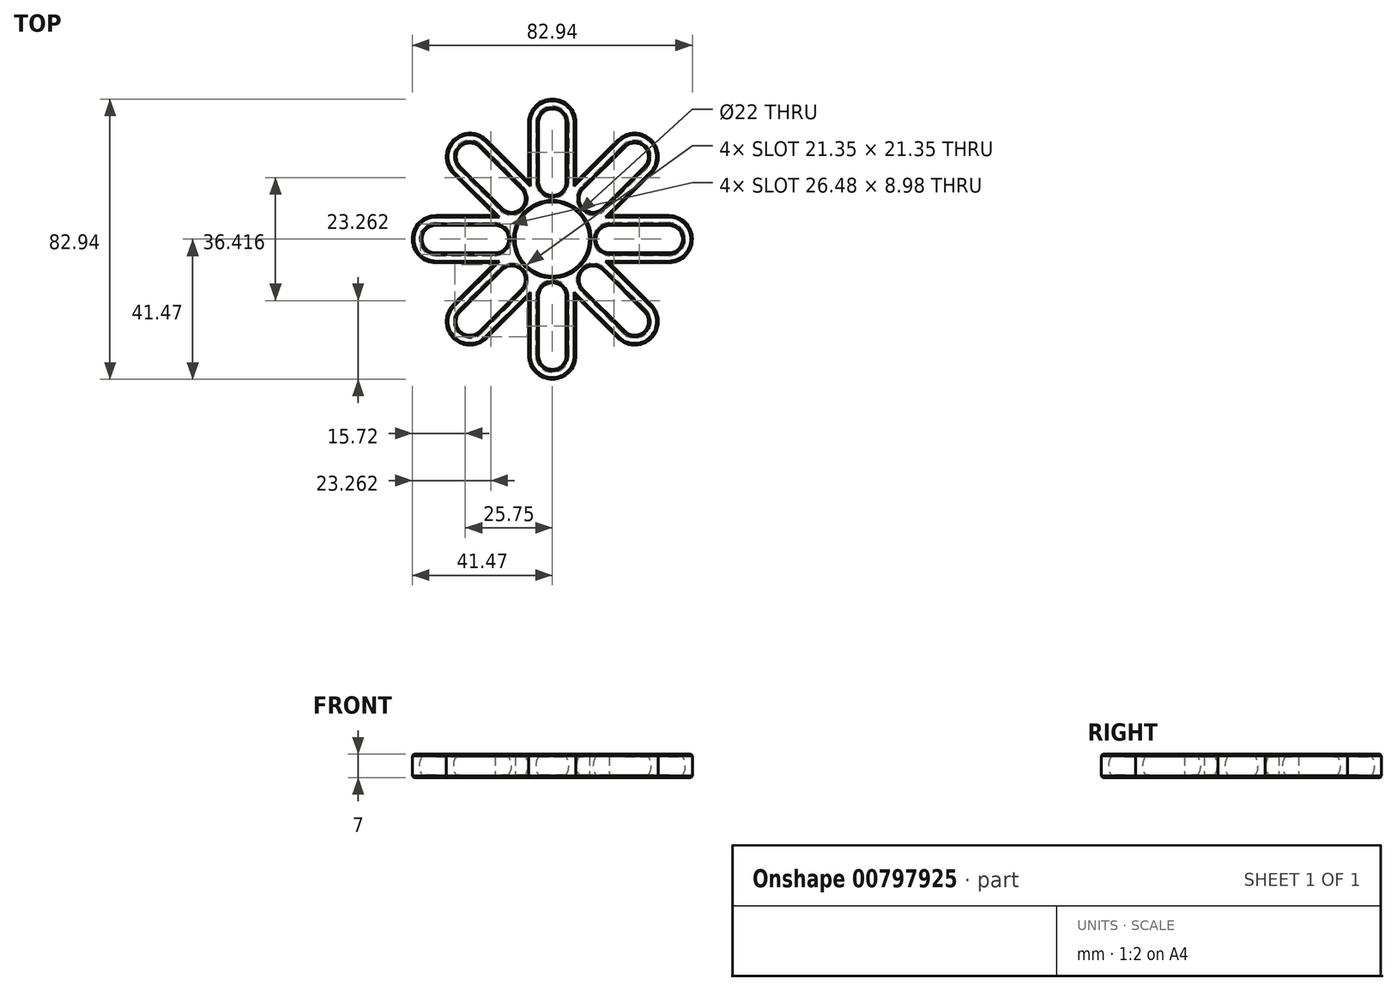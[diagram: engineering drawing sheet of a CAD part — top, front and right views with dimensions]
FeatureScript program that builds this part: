
annotation { "Feature Type Name" : "Feature", "Feature Type Description" : "" }
export const myFeature = defineFeature(function(context is Context, id is Id, definition is map)
    precondition{}
    {
        {
            var Q0;
            Q0=qCreatedBy(makeId("Top.planeOp"),FACE);
            var sketch = newSketch(context, id + "F0", { "sketchPlane" : qUnion([Q0])});
            skArc(sketch, "E0", {"start": v(7, 8.49) * mm, "mid": v(0, 11) * mm, "end": v(-7, 8.49) * mm});
            skArc(sketch, "E1", {"start": v(7, 12.12) * mm, "mid": v(0, 14) * mm, "end": v(-7, 12.12) * mm});
            skPoint(sketch, "E2", {"position": v(0, -24.5) * mm});
            skLineSegment(sketch, "E3", {"start": v(-7, 12.12) * mm, "end": v(-7, 34.47) * mm});
            skLineSegment(sketch, "E4", {"start": v(-7, 34.47) * mm, "end": v(7, 34.47) * mm});
            skLineSegment(sketch, "E5", {"start": v(7, 34.47) * mm, "end": v(7, 12.12) * mm});
            skArc(sketch, "E6", {"start": v(7, 34.47) * mm, "mid": v(0, 41.47) * mm, "end": v(-7, 34.47) * mm});
            skLineSegment(sketch, "E7", {"start": v(7, 12.12) * mm, "end": v(7, 8.49) * mm});
            skLineSegment(sketch, "E8", {"start": v(-7, 12.12) * mm, "end": v(-7, 8.49) * mm});
            skLineSegment(sketch, "E9", {"start": v(0, 0) * mm, "end": v(0, 68.94) * mm, "construction": true});
            skSolve(sketch);
        }
        {
            var Q0;
            Q0=makeQuery(id+"F0.imprint","IMPRINT",FACE,{"disambiguationData":[TD([[makeQuery(id+"F0.imprint","IMPRINT",EDGE,{"derivedFrom":sQuery(id+"F0.wireOp",EDGE,"E0")}),-1.0]])]});
            var Q1;
            {var subQ0=sQuery(id+"F0.wireOp",EDGE,"E3");Q1=makeQuery(id+"F0.imprint","IMPRINT",FACE,{"disambiguationData":[TD([[makeQuery(id+"F0.imprint","IMPRINT",EDGE,{"derivedFrom":subQ0}),-1.0]])]});}
            var Q2;
            Q2=makeQuery(id+"F0.imprint","IMPRINT",FACE,{"disambiguationData":[TD([[makeQuery(id+"F0.imprint","IMPRINT",EDGE,{"derivedFrom":sQuery(id+"F0.wireOp",EDGE,"E4")}),1.0]])]});
            extrude(context, id + "F1", {"entities" : qUnion([Q0, Q1, Q2]), "endBound" : BoundingType.SYMMETRIC, "depth" : 7 * mm, "offsetDistance" : 25 * mm});
        }
        {
            var Q0;
            Q0=qCreatedBy(makeId("Front.planeOp"),FACE);
            var sketch = newSketch(context, id + "F2", { "sketchPlane" : qUnion([Q0])});
            skLineSegment(sketch, "E10", {"start": v(0, 4.9) * mm, "end": v(0, -4.9) * mm});
            skArc(sketch, "E11", {"start": v(0, -4.9) * mm, "mid": v(4.9, 0) * mm, "end": v(0, 4.9) * mm});
            skArc(sketch, "E12.MirrorCS", {"start": v(0, -4.9) * mm, "mid": v(-4.9, 0) * mm, "end": v(0, 4.9) * mm});
            skSolve(sketch);
        }
        {
            var Q0;
            Q0=qSketchRegion(id+"F2",true);
            extrude(context, id + "F3", {"entities" : qUnion([Q0]), "operationType" : NewBodyOperationType.REMOVE, "oppositeDirection" : true, "depth" : 34.5 * mm, "offsetDistance" : 25 * mm, "hasSecondDirection" : true, "secondDirectionOppositeDirection" : true, "secondDirectionDepth" : 17 * mm});
        }
        {
            var Q0;
            Q0=makeQuery(id+"F3.boolean.opBoolean","COPY",FACE,{"derivedFrom":makeQuery(id+"F3.opExtrude","CAP_FACE",FACE,{"disambiguationData":[OSD([sQuery(id+"F2.wireOp",EDGE,"E11"),sQuery(id+"F2.wireOp",EDGE,"E12.MirrorCS")])],"isStart":false})});
            var sketch = newSketch(context, id + "F4", { "sketchPlane" : qUnion([Q0])});
            skArc(sketch, "E13", {"start": v(0, -4.9) * mm, "mid": v(4.9, 0) * mm, "end": v(0, 4.9) * mm});
            skLineSegment(sketch, "E14", {"start": v(0, -4.9) * mm, "end": v(0, 4.9) * mm});
            skSolve(sketch);
        }
        {
            var Q0;
            Q0=qSketchRegion(id+"F4",true);
            var Q1;
            Q1=sQuery(id+"F4.wireOp",EDGE,"E14");
            revolve(context, id + "F5", {"operationType" : NewBodyOperationType.REMOVE, "surfaceOperationType" : NewSurfaceOperationType.NEW, "entities" : qUnion([Q0]), "axis" : qUnion([Q1]), "revolveType" : RevolveType.FULL});
        }
        {
            var Q0;
            Q0=makeQuery(id+"F3.boolean.opBoolean","COPY",FACE,{"derivedFrom":makeQuery(id+"F3.opExtrude","CAP_FACE",FACE,{"disambiguationData":[OSD([sQuery(id+"F2.wireOp",EDGE,"E11"),sQuery(id+"F2.wireOp",EDGE,"E12.MirrorCS")])],"isStart":true})});
            var sketch = newSketch(context, id + "F6", { "sketchPlane" : qUnion([Q0])});
            skArc(sketch, "E15", {"start": v(0, -4.9) * mm, "mid": v(4.9, 0) * mm, "end": v(0, 4.9) * mm});
            skLineSegment(sketch, "E16", {"start": v(0, 4.9) * mm, "end": v(0, -4.9) * mm});
            skSolve(sketch);
        }
        {
            var Q0;
            Q0=qSketchRegion(id+"F6",true);
            var Q1;
            Q1=sQuery(id+"F6.wireOp",EDGE,"E16");
            revolve(context, id + "F7", {"operationType" : NewBodyOperationType.REMOVE, "surfaceOperationType" : NewSurfaceOperationType.NEW, "entities" : qUnion([Q0]), "axis" : qUnion([Q1]), "revolveType" : RevolveType.FULL, "oppositeDirection" : true});
        }
        {
            var Q0;
            Q0=makeQuery(id+"F1.opExtrude","SWEPT_BODY",BODY,{"disambiguationData":[OSD([sQuery(id+"F0.wireOp",EDGE,"E0"),sQuery(id+"F0.wireOp",EDGE,"E1"),sQuery(id+"F0.wireOp",EDGE,"E3"),sQuery(id+"F0.wireOp",EDGE,"E5"),sQuery(id+"F0.wireOp",EDGE,"E6")])]});
            var Q1;
            Q1=sQuery(id+"F2.wireOp",EDGE,"E10");
            circularPattern(context, id + "F8", {"operationType" : NewBodyOperationType.ADD, "entities" : qUnion([Q0]), "axis" : qUnion([Q1]), "angle" : 360 * degree, "instanceCount" : 8, "equalSpace" : true});
        }
        {
            var Q0;
            {var subQ0=makeQuery(id+"F1.opExtrude","CAP_FACE",FACE,{"disambiguationData":[OSD([sQuery(id+"F0.wireOp",EDGE,"E0"),sQuery(id+"F0.wireOp",EDGE,"E3"),sQuery(id+"F0.wireOp",EDGE,"E5"),sQuery(id+"F0.wireOp",EDGE,"E6"),sQuery(id+"F0.wireOp",EDGE,"E7"),sQuery(id+"F0.wireOp",EDGE,"E8")])],"isStart":false});Q0=makeQuery(id+"F8.boolean.opBoolean","MERGE",FACE,{"derivedFrom":[subQ0,makeQuery(id+"F8.opPattern","COPY",FACE,{"derivedFrom":subQ0,"instanceName":"1"}),makeQuery(id+"F8.opPattern","COPY",FACE,{"derivedFrom":subQ0,"instanceName":"2"}),makeQuery(id+"F8.opPattern","COPY",FACE,{"derivedFrom":subQ0,"instanceName":"3"}),makeQuery(id+"F8.opPattern","COPY",FACE,{"derivedFrom":subQ0,"instanceName":"4"}),makeQuery(id+"F8.opPattern","COPY",FACE,{"derivedFrom":subQ0,"instanceName":"5"}),makeQuery(id+"F8.opPattern","COPY",FACE,{"derivedFrom":subQ0,"instanceName":"6"}),makeQuery(id+"F8.opPattern","COPY",FACE,{"derivedFrom":subQ0,"instanceName":"7"})]});}
            var Q1;
            {var subQ0=makeQuery(id+"F1.opExtrude","CAP_FACE",FACE,{"disambiguationData":[OSD([sQuery(id+"F0.wireOp",EDGE,"E0"),sQuery(id+"F0.wireOp",EDGE,"E3"),sQuery(id+"F0.wireOp",EDGE,"E5"),sQuery(id+"F0.wireOp",EDGE,"E6"),sQuery(id+"F0.wireOp",EDGE,"E7"),sQuery(id+"F0.wireOp",EDGE,"E8")])],"isStart":true});Q1=makeQuery(id+"F8.boolean.opBoolean","MERGE",FACE,{"derivedFrom":[subQ0,makeQuery(id+"F8.opPattern","COPY",FACE,{"derivedFrom":subQ0,"instanceName":"1"}),makeQuery(id+"F8.opPattern","COPY",FACE,{"derivedFrom":subQ0,"instanceName":"2"}),makeQuery(id+"F8.opPattern","COPY",FACE,{"derivedFrom":subQ0,"instanceName":"3"}),makeQuery(id+"F8.opPattern","COPY",FACE,{"derivedFrom":subQ0,"instanceName":"4"}),makeQuery(id+"F8.opPattern","COPY",FACE,{"derivedFrom":subQ0,"instanceName":"5"}),makeQuery(id+"F8.opPattern","COPY",FACE,{"derivedFrom":subQ0,"instanceName":"6"}),makeQuery(id+"F8.opPattern","COPY",FACE,{"derivedFrom":subQ0,"instanceName":"7"})]});}
            chamfer(context, id + "F9", {"entities" : qUnion([Q0, Q1]), "width" : .5 * mm, "tangentPropagation" : true});
        }
    });
